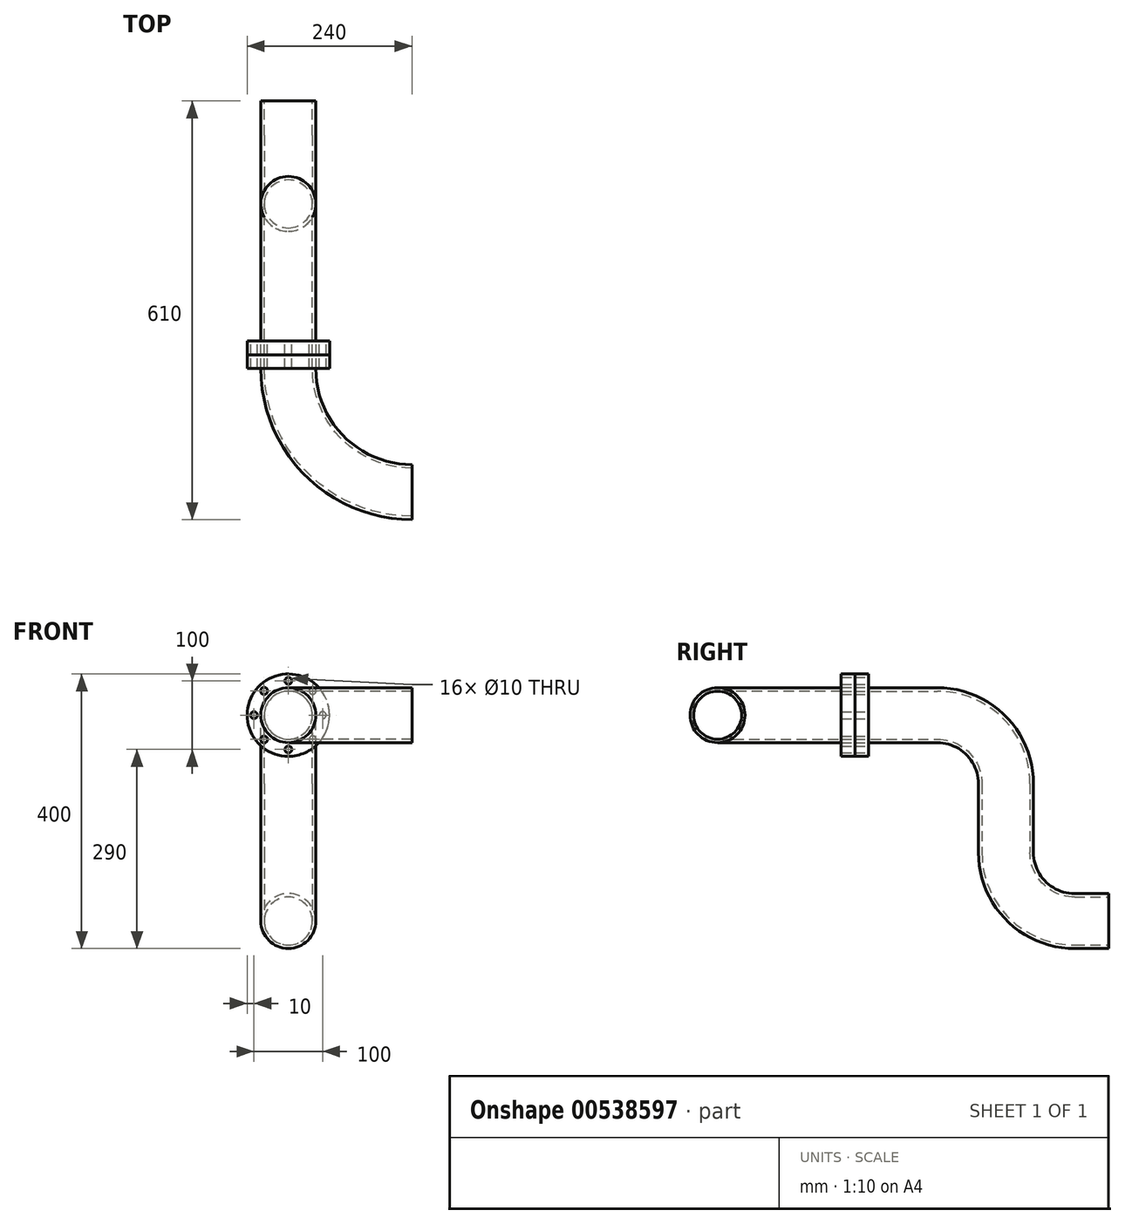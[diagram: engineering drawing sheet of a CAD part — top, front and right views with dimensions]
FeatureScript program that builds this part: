
annotation { "Feature Type Name" : "Feature", "Feature Type Description" : "" }
export const myFeature = defineFeature(function(context is Context, id is Id, definition is map)
    precondition{}
    {
        {
            var Q0;
            Q0=qCreatedBy(makeId("Front.planeOp"),FACE);
            var sketch = newSketch(context, id + "F0", { "sketchPlane" : qUnion([Q0])});
            skCircle(sketch, "E0", {"center": v(0, 0) * mm, "radius": 60 * mm});
            skCircle(sketch, "E1", {"center": v(0, 50) * mm, "radius": 5 * mm});
            skCircle(sketch, "E2.1.0", {"center": v(-35.36, 35.36) * mm, "radius": 5 * mm});
            skCircle(sketch, "E2.2.0", {"center": v(-50, 0) * mm, "radius": 5 * mm});
            skCircle(sketch, "E2.3.0", {"center": v(-35.36, -35.36) * mm, "radius": 5 * mm});
            skCircle(sketch, "E2.4.0", {"center": v(0, -50) * mm, "radius": 5 * mm});
            skCircle(sketch, "E2.5.0", {"center": v(35.36, -35.36) * mm, "radius": 5 * mm});
            skCircle(sketch, "E2.6.0", {"center": v(50, 0) * mm, "radius": 5 * mm});
            skCircle(sketch, "E2.7.0", {"center": v(35.36, 35.36) * mm, "radius": 5 * mm});
            skCircle(sketch, "E3", {"center": v(0, 0) * mm, "radius": 35 * mm});
            skSolve(sketch);
        }
        {
            var Q0;
            Q0 = qSketchRegion(id + "F0", true);
            extrude(context, id + "F1", {"entities" : qUnion([Q0]), "depth" : 20 * mm, "offsetDistance" : 25 * mm});
        }
        {
            var Q0;
            Q0=qCreatedBy(makeId("Front.planeOp"),FACE);
            var sketch = newSketch(context, id + "F2", { "sketchPlane" : qUnion([Q0])});
            skCircle(sketch, "E4", {"center": v(0, 0) * mm, "radius": 35 * mm});
            skCircle(sketch, "E5", {"center": v(0, 0) * mm, "radius": 40 * mm});
            skSolve(sketch);
        }
        {
            var Q0;
            Q0=qCreatedBy(makeId("Right.planeOp"),FACE);
            var sketch = newSketch(context, id + "F3", { "sketchPlane" : qUnion([Q0])});
            skLineSegment(sketch, "E6", {"start": v(0, 0) * mm, "end": v(100, 0) * mm});
            skLineSegment(sketch, "E7", {"start": v(200, -100) * mm, "end": v(200, -200) * mm});
            skLineSegment(sketch, "E8", {"start": v(300, -300) * mm, "end": v(350, -300) * mm});
            skPoint(sketch, "E9.visualSharp", {"position": v(200, 0) * mm});
            skArc(sketch, "E9.filletArc", {"start": v(200, -100) * mm, "mid": v(170.71, -29.29) * mm, "end": v(100, 0) * mm});
            skPoint(sketch, "E10.visualSharp", {"position": v(200, -300) * mm});
            skArc(sketch, "E10.filletArc", {"start": v(200, -200) * mm, "mid": v(229.29, -270.71) * mm, "end": v(300, -300) * mm});
            skSolve(sketch);
        }
        {
            var Q0;
            Q0=makeQuery(id+"F2.imprint","IMPRINT",FACE,{"disambiguationData":[TD([[makeQuery(id+"F2.imprint","IMPRINT",EDGE,{"derivedFrom":sQuery(id+"F2.wireOp",EDGE,"E4")}),-1.0]])]});
            var Q1;
            Q1=sQuery(id+"F3.wireOp",EDGE,"E6");
            var Q2;
            Q2=sQuery(id+"F3.wireOp",EDGE,"E7");
            var Q3;
            Q3=sQuery(id+"F3.wireOp",EDGE,"E8");
            var Q4;
            Q4=sQuery(id+"F3.wireOp",EDGE,"E9.filletArc");
            var Q5;
            Q5=sQuery(id+"F3.wireOp",EDGE,"E10.filletArc");
            sweep(context, id + "F4", {"operationType" : NewBodyOperationType.ADD, "profiles" : qUnion([Q0]), "path" : qUnion([Q1, Q2, Q3, Q4, Q5])});
        }
        {
            var Q0;
            Q0=makeQuery(id+"F1.opExtrude","CAP_FACE",FACE,{"disambiguationData":[OSD([sQuery(id+"F0.wireOp",EDGE,"E0"),sQuery(id+"F0.wireOp",EDGE,"E1"),sQuery(id+"F0.wireOp",EDGE,"E2.1.0"),sQuery(id+"F0.wireOp",EDGE,"E2.2.0"),sQuery(id+"F0.wireOp",EDGE,"E2.3.0"),sQuery(id+"F0.wireOp",EDGE,"E2.4.0"),sQuery(id+"F0.wireOp",EDGE,"E2.5.0"),sQuery(id+"F0.wireOp",EDGE,"E2.6.0"),sQuery(id+"F0.wireOp",EDGE,"E2.7.0"),sQuery(id+"F0.wireOp",EDGE,"E3")])],"isStart":false});
            extrude(context, id + "F5", {"entities" : qUnion([Q0]), "depth" : 20 * mm, "offsetDistance" : 25 * mm});
        }
        {
            var Q0;
            Q0=makeQuery(id+"F5.opExtrude","CAP_FACE",FACE,{"disambiguationData":[OSD([sQuery(id+"F0.wireOp",EDGE,"E0"),sQuery(id+"F0.wireOp",EDGE,"E1"),sQuery(id+"F0.wireOp",EDGE,"E2.1.0"),sQuery(id+"F0.wireOp",EDGE,"E2.2.0"),sQuery(id+"F0.wireOp",EDGE,"E2.3.0"),sQuery(id+"F0.wireOp",EDGE,"E2.4.0"),sQuery(id+"F0.wireOp",EDGE,"E2.5.0"),sQuery(id+"F0.wireOp",EDGE,"E2.6.0"),sQuery(id+"F0.wireOp",EDGE,"E2.7.0"),sQuery(id+"F0.wireOp",EDGE,"E3")])],"isStart":false});
            var sketch = newSketch(context, id + "F6", { "sketchPlane" : qUnion([Q0])});
            skCircle(sketch, "E11", {"center": v(0, 0) * mm, "radius": 35 * mm});
            skCircle(sketch, "E12", {"center": v(0, 0) * mm, "radius": 40 * mm});
            skLineSegment(sketch, "E13", {"start": v(180, 80.38) * mm, "end": v(180, -77.34) * mm, "construction": true});
            skSolve(sketch);
        }
        {
            var Q0;
            Q0=makeQuery(id+"F6.imprint","IMPRINT",FACE,{"disambiguationData":[TD([[makeQuery(id+"F6.imprint","IMPRINT",EDGE,{"derivedFrom":sQuery(id+"F6.wireOp",EDGE,"E11")}),-1.0]])]});
            var Q1;
            Q1=sQuery(id+"F6.wireOp",EDGE,"E13");
            revolve(context, id + "F7", {"operationType" : NewBodyOperationType.ADD, "entities" : qUnion([Q0]), "axis" : qUnion([Q1]), "revolveType" : RevolveType.ONE_DIRECTION, "oppositeDirection" : true, "angle" : 90 * degree});
        }
    });
